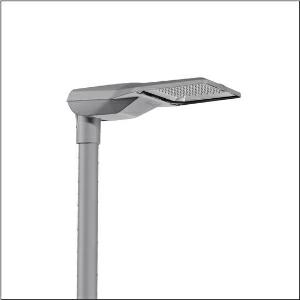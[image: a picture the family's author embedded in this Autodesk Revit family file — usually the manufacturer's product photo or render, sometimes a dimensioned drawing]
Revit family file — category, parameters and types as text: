
# Revit family: streetlight_sl_21_iq_midi___stw1_0a_5xe3e61d08nb_dcea
name_source: partatom
category: Lighting Fixtures
units: mm (PartAtom-declared; Revit-internal decimal feet)

## family parameters
Cut with Voids When Loaded = No
Host = Face
Light Source = No
Part Type = Normal
Room Calculation Point = No
Round Connector Dimension = Use Diameter
Shared = No

## types (1)
- --- (1 x LED, 20820 lm, 155.5 W, 2700K)
    Apparent Load = 155 VA
    CIE Flux Codes = 39 75 98 100 100
    Color Rendering = 70
    Color Temperature = 2700K
    Default Elevation = 1800 mm
    Description = Streetlight SL 21 iQ midi, mast luminaire, primary light control with lens, of PMMA, primary optical cover: cover, of toughened safety glass, transparent, light distribution: STW1.0a, light emission: direct distribution, primary light characteristic: asymmetric, installation type: post-top, side-entry, LED, High Power LED, rated luminous flux: 20.820lm, luminous efficacy: 134lm/W, light colour: 727, colour temperature: 2700K, control: Auto-Match, Temp-Guard, Lumen-Switch, Night-Set, Smart-Wire, Light-Fading, Desk-Remote (wireless, voltage-free reading and setting of iQ features in the workshop via application-optimized NFC function/RFID function), optimised constant luminous flux control (CLO 2.0), presetting dimming linear, mains connection: 230..240V, AC, 50/60Hz, start of lifetime: 156W, end of service life: 162W, reduction: 69W, luminaire housing, of diecast aluminium, powder-coated, Siteco® metallic grey (DB 702S), corrosivity category C5 mid according to DIN EN ISO 12944, please order mast flange separately, inclination adjustable: 0°, 5°, 10°, 15°, sealing non-destructively replaceable, multi-level sealing system, length: 644mm, width: 335mm, height: 110mm, mast flange for spigot size: 42mm (side-entry): 5XC10008XM4, 60/48mm (side-entry/post-top): 5XC10108XM2, 76/60mm (side-entry/post-top): 5XC10108XM1, protection rating (complete): IP66, insulation class (complete): insulation class II (safety insulation), certification: CE, ENEC, ENEC+, VDE, impact resistance: IK09, permissible operating ambient temperature for outdoor applications: -40..+50°C, standard-compliant lighting for roads and squares, packaging unit: 1 piece

Light Distribution: STW1.0a
    Height = 111 mm
    Lamp = 1 x LED
    Lamp Light Flux = 20820 lm
    Lamp Power = 155.5 W
    Lamp count = 1
    Length = 644 mm
    Luminous efficacy = 134 lm/W
    Manufacturer = Siteco
    ModVariant = No
    Model = 5XE3E61D08NB
    Number of Poles = 1
    OnlyDefault = Yes
    Power Factor = 1
    Product Name = Streetlight SL 21 iQ midi | STW1.0a
    Product group = mast luminaire | pylon top
    ProductGroupID = 6100
    Protection Class = Protection class II
    Protection Degree = IP 66
    RLX_Detail_Level = 1
    RLX_Emergency_Light_Flux = 0 lm
    RLX_Emergency_Type = 0
    RLX_Emergency_Type_DB = No
    RlxData = <blob elided: 90969 chars, md5=d86d6a98>
    Socket = socket
    Standby Power = 0 W
    System Light Flux = 20820 lm
    System Power = 155 W
    Type Comments = factory setting: luminous flux: 100 % | dim-lin: 254 | 823 mA
    Type Image = l_1004298.jpg
    URL = http://relux.com
    VarID = @adj_102345
    Voltage = 0 V
    Weight = 0.00 kg
    Width = 336 mm

## geometry (parser evidence)
native form markers: Blend x4, Sweep x12
no freeform markers — native parametric forms only
